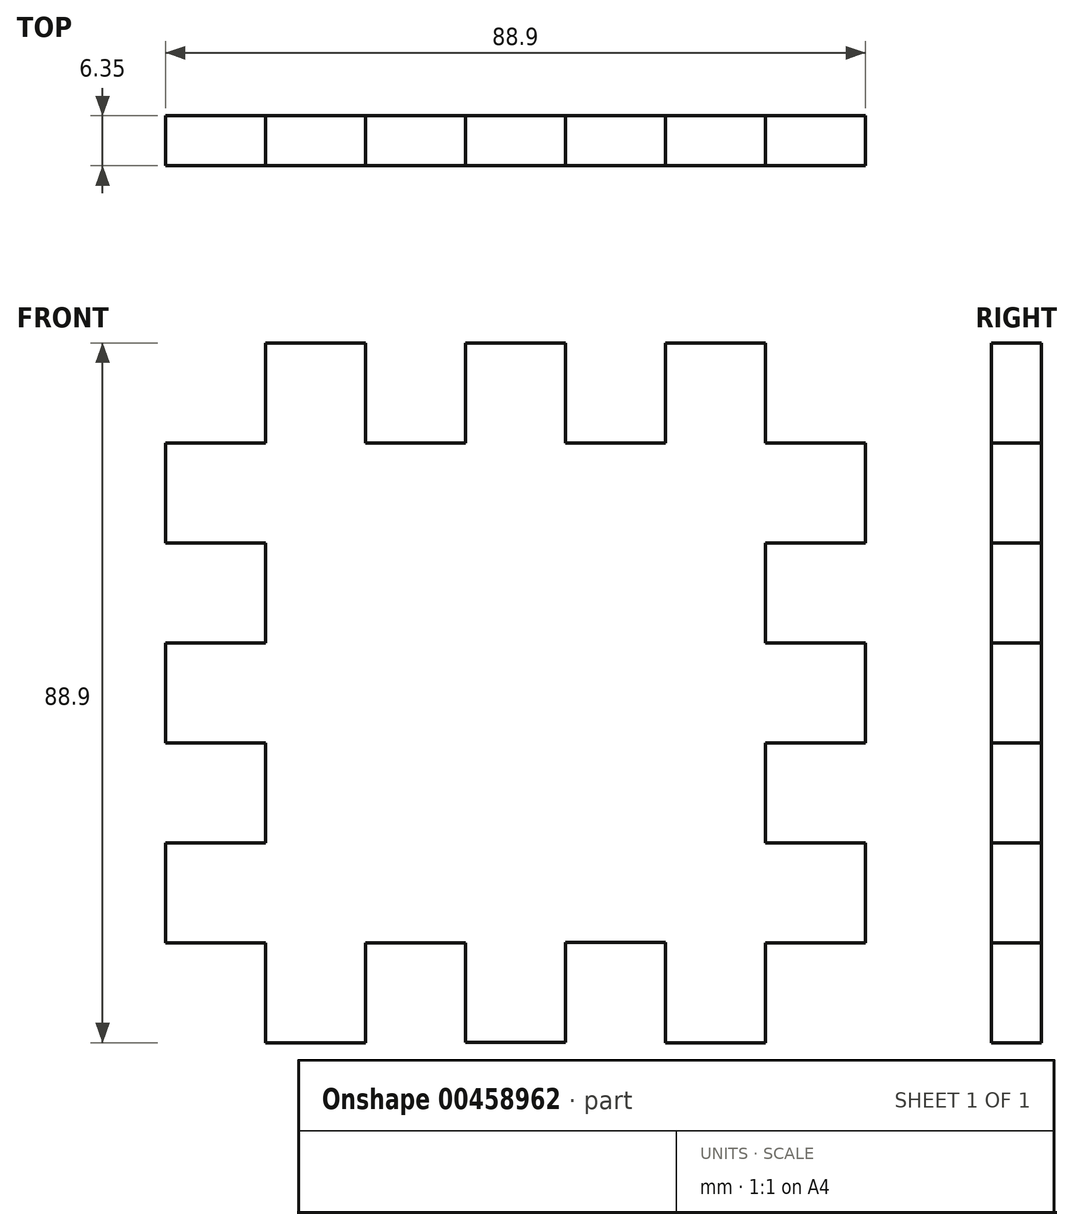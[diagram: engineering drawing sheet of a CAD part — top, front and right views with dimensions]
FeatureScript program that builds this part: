
annotation { "Feature Type Name" : "Feature", "Feature Type Description" : "" }
export const myFeature = defineFeature(function(context is Context, id is Id, definition is map)
    precondition{}
    {
        {
            var Q0;
            Q0=qCreatedBy(makeId("Front.planeOp"),FACE);
            var sketch = newSketch(context, id + "F0", { "sketchPlane" : qUnion([Q0])});
            skLineSegment(sketch, "E0", {"start": v(0, 33.71) * mm, "end": v(-12.7, 33.71) * mm});
            skLineSegment(sketch, "E1", {"start": v(-12.7, 33.71) * mm, "end": v(-12.7, 21.01) * mm});
            skLineSegment(sketch, "E2", {"start": v(-12.7, 21.01) * mm, "end": v(-25.4, 21.01) * mm});
            skLineSegment(sketch, "E3", {"start": v(-25.4, 21.01) * mm, "end": v(-25.4, 33.71) * mm});
            skLineSegment(sketch, "E4", {"start": v(-25.4, 33.71) * mm, "end": v(-38.1, 33.71) * mm});
            skLineSegment(sketch, "E5", {"start": v(-38.1, 33.71) * mm, "end": v(-38.1, 21.01) * mm});
            skLineSegment(sketch, "E6", {"start": v(-38.1, 21.01) * mm, "end": v(-50.8, 21.01) * mm});
            skLineSegment(sketch, "E7", {"start": v(-50.8, 21.01) * mm, "end": v(-50.8, 33.71) * mm});
            skLineSegment(sketch, "E8", {"start": v(-50.8, 33.71) * mm, "end": v(-63.5, 33.71) * mm});
            skLineSegment(sketch, "E9", {"start": v(-63.5, 33.71) * mm, "end": v(-63.5, 21.01) * mm});
            skLineSegment(sketch, "E10", {"start": v(-63.5, 21.01) * mm, "end": v(-76.2, 21.01) * mm});
            skLineSegment(sketch, "E11", {"start": v(-76.2, 21.01) * mm, "end": v(-76.2, 8.31) * mm});
            skLineSegment(sketch, "E12", {"start": v(-76.2, 8.31) * mm, "end": v(-63.5, 8.31) * mm});
            skLineSegment(sketch, "E13", {"start": v(-63.5, 8.31) * mm, "end": v(-63.5, -4.39) * mm});
            skLineSegment(sketch, "E14", {"start": v(-63.5, -4.39) * mm, "end": v(-76.2, -4.39) * mm});
            skLineSegment(sketch, "E15", {"start": v(-76.2, -4.39) * mm, "end": v(-76.2, -17.09) * mm});
            skLineSegment(sketch, "E16", {"start": v(-76.2, -17.09) * mm, "end": v(-63.5, -17.09) * mm});
            skLineSegment(sketch, "E17", {"start": v(-63.5, -17.09) * mm, "end": v(-63.5, -29.79) * mm});
            skLineSegment(sketch, "E18", {"start": v(-63.5, -29.79) * mm, "end": v(-76.2, -29.79) * mm});
            skLineSegment(sketch, "E19", {"start": v(-76.2, -29.79) * mm, "end": v(-76.2, -42.49) * mm});
            skLineSegment(sketch, "E20", {"start": v(-76.2, -42.49) * mm, "end": v(-63.5, -42.49) * mm});
            skLineSegment(sketch, "E21", {"start": v(-63.5, -42.49) * mm, "end": v(-63.5, -55.19) * mm});
            skLineSegment(sketch, "E22", {"start": v(-63.5, -55.19) * mm, "end": v(-50.8, -55.19) * mm});
            skLineSegment(sketch, "E23", {"start": v(-50.8, -55.19) * mm, "end": v(-50.8, -42.49) * mm});
            skLineSegment(sketch, "E24", {"start": v(-50.8, -42.49) * mm, "end": v(-38.1, -42.49) * mm});
            skLineSegment(sketch, "E25", {"start": v(-38.1, -42.49) * mm, "end": v(-38.1, -55.14) * mm});
            skLineSegment(sketch, "E26", {"start": v(-38.1, -55.14) * mm, "end": v(-25.4, -55.14) * mm});
            skLineSegment(sketch, "E27", {"start": v(-25.4, -55.14) * mm, "end": v(-25.4, -42.44) * mm});
            skLineSegment(sketch, "E28", {"start": v(-25.4, -42.44) * mm, "end": v(-12.7, -42.44) * mm});
            skLineSegment(sketch, "E29", {"start": v(0, 33.71) * mm, "end": v(0, 21.01) * mm});
            skLineSegment(sketch, "E30", {"start": v(0, 21.01) * mm, "end": v(12.7, 21.01) * mm});
            skLineSegment(sketch, "E31", {"start": v(12.7, 21.01) * mm, "end": v(12.7, 8.31) * mm});
            skLineSegment(sketch, "E32", {"start": v(12.7, 8.31) * mm, "end": v(0, 8.31) * mm});
            skLineSegment(sketch, "E33", {"start": v(0, 8.31) * mm, "end": v(0, -4.39) * mm});
            skLineSegment(sketch, "E34", {"start": v(0, -4.39) * mm, "end": v(12.7, -4.39) * mm});
            skLineSegment(sketch, "E35", {"start": v(12.7, -4.39) * mm, "end": v(12.7, -17.09) * mm});
            skLineSegment(sketch, "E36", {"start": v(12.7, -17.09) * mm, "end": v(0, -17.09) * mm});
            skLineSegment(sketch, "E37", {"start": v(0, -17.09) * mm, "end": v(0, -29.79) * mm});
            skLineSegment(sketch, "E38", {"start": v(0, -29.79) * mm, "end": v(12.7, -29.79) * mm});
            skLineSegment(sketch, "E39", {"start": v(12.7, -42.49) * mm, "end": v(12.7, -29.79) * mm});
            skLineSegment(sketch, "E40", {"start": v(12.7, -42.49) * mm, "end": v(0, -42.49) * mm});
            skLineSegment(sketch, "E41", {"start": v(0, -42.49) * mm, "end": v(0, -55.19) * mm});
            skLineSegment(sketch, "E42", {"start": v(0, -55.19) * mm, "end": v(-12.7, -55.19) * mm});
            skLineSegment(sketch, "E43", {"start": v(-12.7, -55.19) * mm, "end": v(-12.7, -42.44) * mm});
            skSolve(sketch);
        }
        {
            var Q0;
            Q0=makeQuery(id+"F0.imprint","IMPRINT",FACE,{"disambiguationData":[TD([[makeQuery(id+"F0.imprint","IMPRINT",EDGE,{"derivedFrom":sQuery(id+"F0.wireOp",EDGE,"E0")}),1.0]])]});
            extrude(context, id + "F1", {"entities" : qUnion([Q0]), "depth" : 6.35 * mm});
        }
    });
